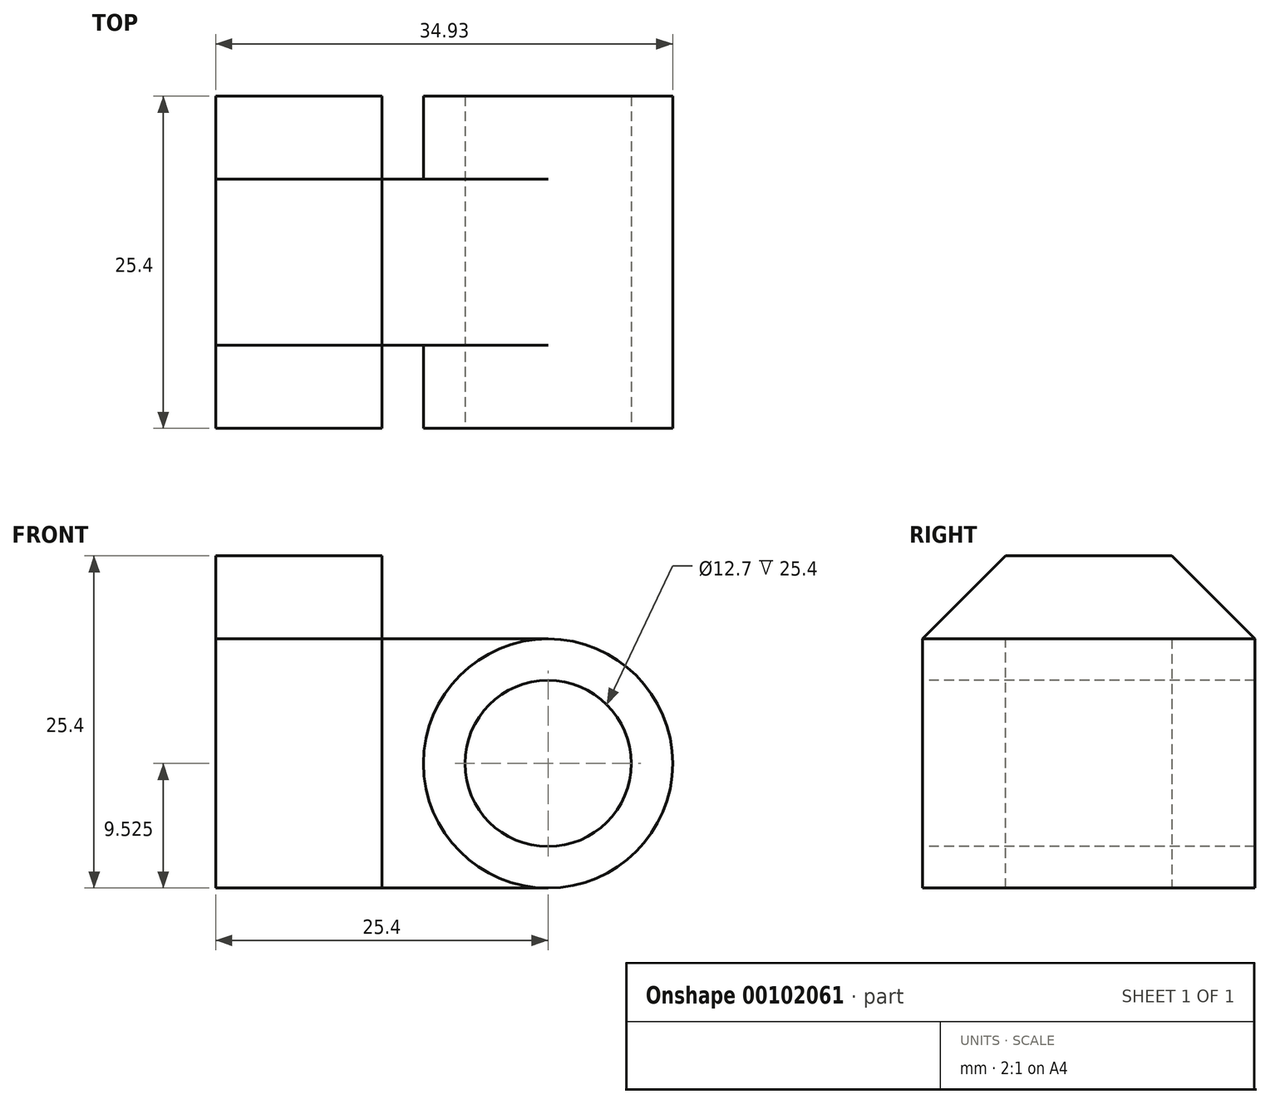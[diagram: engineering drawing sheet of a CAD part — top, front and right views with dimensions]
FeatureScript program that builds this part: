
annotation { "Feature Type Name" : "Feature", "Feature Type Description" : "" }
export const myFeature = defineFeature(function(context is Context, id is Id, definition is map)
    precondition{}
    {
        {
            var Q0;
            Q0=qCreatedBy(makeId("Right.planeOp"),FACE);
            var sketch = newSketch(context, id + "F0", { "sketchPlane" : qUnion([Q0])});
            skLineSegment(sketch, "E0.bottom", {"start": v(0, 0) * mm, "end": v(25.4, 0) * mm});
            skLineSegment(sketch, "E0.top", {"start": v(0, 25.4) * mm, "end": v(25.4, 25.4) * mm});
            skLineSegment(sketch, "E0.left", {"start": v(0, 0) * mm, "end": v(0, 25.4) * mm});
            skLineSegment(sketch, "E0.right", {"start": v(25.4, 0) * mm, "end": v(25.4, 25.4) * mm});
            skLineSegment(sketch, "E1", {"start": v(0, 25.4) * mm, "end": v(6.35, 25.4) * mm});
            skLineSegment(sketch, "E2", {"start": v(6.35, 25.4) * mm, "end": v(0, 19.05) * mm});
            skLineSegment(sketch, "E3", {"start": v(0, 19.05) * mm, "end": v(0, 25.4) * mm});
            skLineSegment(sketch, "E4", {"start": v(25.4, 25.4) * mm, "end": v(19.05, 25.4) * mm});
            skLineSegment(sketch, "E5", {"start": v(19.05, 25.4) * mm, "end": v(25.4, 19.05) * mm});
            skLineSegment(sketch, "E6", {"start": v(25.4, 19.05) * mm, "end": v(25.4, 25.4) * mm});
            skSolve(sketch);
        }
        {
            var Q0;
            Q0=makeQuery(id+"F0.imprint","IMPRINT",FACE,{"disambiguationData":[TD([[makeQuery(id+"F0.imprint","IMPRINT",EDGE,{"derivedFrom":sQuery(id+"F0.wireOp",EDGE,"E0.bottom")}),1.0]])]});
            extrude(context, id + "F1", {"entities" : qUnion([Q0]), "depth" : 12.7 * mm});
        }
        {
            var Q0;
            Q0=qCreatedBy(makeId("Right.planeOp"),FACE);
            var sketch = newSketch(context, id + "F2", { "sketchPlane" : qUnion([Q0])});
            skLineSegment(sketch, "E7", {"start": v(6.35, 0) * mm, "end": v(19.05, 0) * mm});
            skLineSegment(sketch, "E8", {"start": v(19.05, 0) * mm, "end": v(19.05, 19.05) * mm});
            skLineSegment(sketch, "E9", {"start": v(19.05, 19.05) * mm, "end": v(6.35, 19.05) * mm});
            skLineSegment(sketch, "E10", {"start": v(6.35, 19.05) * mm, "end": v(6.35, 0) * mm});
            skSolve(sketch);
        }
        {
            var Q0;
            Q0 = qSketchRegion(id + "F2", true);
            extrude(context, id + "F3", {"entities" : qUnion([Q0]), "operationType" : NewBodyOperationType.ADD, "depth" : 25.4 * mm});
        }
        {
            var Q0;
            Q0=qCreatedBy(makeId("Front.planeOp"),FACE);
            var sketch = newSketch(context, id + "F4", { "sketchPlane" : qUnion([Q0])});
            skCircle(sketch, "E11", {"center": v(25.4, 9.53) * mm, "radius": 9.53 * mm});
            skSolve(sketch);
        }
        {
            var Q0;
            Q0=makeQuery(id+"F4.imprint","IMPRINT",FACE,{"disambiguationData":[TD([[makeQuery(id+"F4.imprint","IMPRINT",EDGE,{"derivedFrom":sQuery(id+"F4.wireOp",EDGE,"E11")}),1.0]])]});
            extrude(context, id + "F5", {"entities" : qUnion([Q0]), "operationType" : NewBodyOperationType.ADD, "oppositeDirection" : true, "depth" : 25.4 * mm});
        }
        {
            var Q0;
            Q0=qCreatedBy(makeId("Front.planeOp"),FACE);
            var sketch = newSketch(context, id + "F6", { "sketchPlane" : qUnion([Q0])});
            skCircle(sketch, "E12", {"center": v(25.4, 9.53) * mm, "radius": 6.35 * mm});
            skLineSegment(sketch, "E13", {"start": v(0, 0) * mm, "end": v(25.4, 0) * mm, "construction": true});
            skSolve(sketch);
        }
        {
            var Q0;
            Q0 = qSketchRegion(id + "F6", true);
            extrude(context, id + "F7", {"entities" : qUnion([Q0]), "operationType" : NewBodyOperationType.REMOVE, "oppositeDirection" : true, "depth" : 25.4 * mm});
        }
    });
